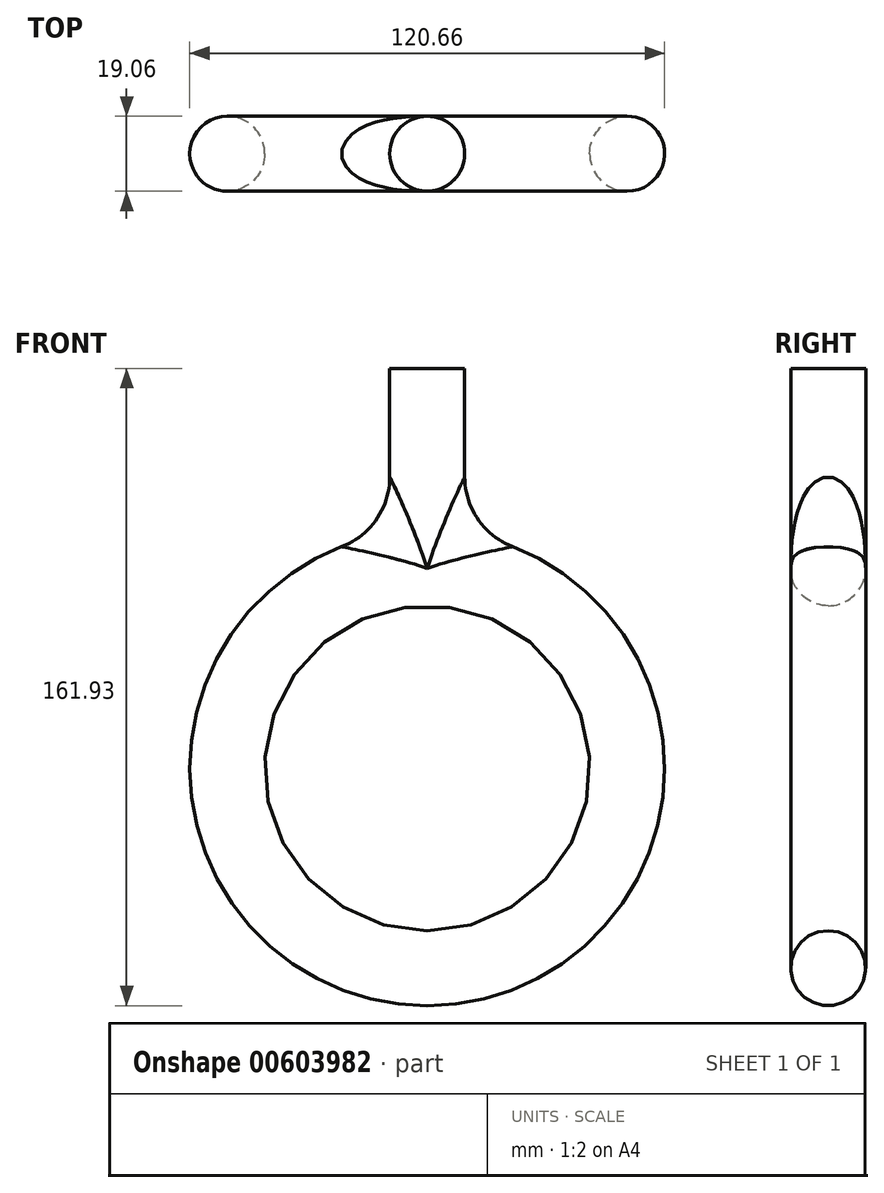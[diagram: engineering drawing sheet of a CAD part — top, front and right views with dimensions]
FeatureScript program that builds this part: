
annotation { "Feature Type Name" : "Feature", "Feature Type Description" : "" }
export const myFeature = defineFeature(function(context is Context, id is Id, definition is map)
    precondition{}
    {
        {
            var Q0;
            Q0=qCreatedBy(makeId("Top.planeOp"),FACE);
            var sketch = newSketch(context, id + "F0", { "sketchPlane" : qUnion([Q0])});
            skCircle(sketch, "E0", {"center": v(0, 0) * mm, "radius": 9.52 * mm});
            skSolve(sketch);
        }
        {
            var Q0;
            Q0 = qSketchRegion(id + "F0", true);
            extrude(context, id + "F1", {"entities" : qUnion([Q0]), "depth" : 50.8 * mm, "offsetDistance" : 25.4 * mm});
        }
        {
            var Q0;
            Q0=qCreatedBy(makeId("Right.planeOp"),FACE);
            var sketch = newSketch(context, id + "F2", { "sketchPlane" : qUnion([Q0])});
            skCircle(sketch, "E1", {"center": v(0, 0) * mm, "radius": 9.53 * mm});
            skSolve(sketch);
        }
        {
            var Q0;
            Q0=qCreatedBy(makeId("Front.planeOp"),FACE);
            var sketch = newSketch(context, id + "F3", { "sketchPlane" : qUnion([Q0])});
            skCircle(sketch, "E2", {"center": v(0, -50.8) * mm, "radius": 50.8 * mm});
            skSolve(sketch);
        }
        {
            var Q0;
            Q0=makeQuery(id+"F2.imprint","IMPRINT",FACE,{"disambiguationData":[TD([[makeQuery(id+"F2.imprint","IMPRINT",EDGE,{"derivedFrom":sQuery(id+"F2.wireOp",EDGE,"E1")}),1.0]])]});
            var Q1;
            Q1=sQuery(id+"F3.wireOp",EDGE,"E2");
            revolve(context, id + "F4", {"operationType" : NewBodyOperationType.ADD, "entities" : qUnion([Q0]), "axis" : qUnion([Q1]), "revolveType" : RevolveType.FULL});
        }
        {
            var Q0;
            Q0=makeQuery(id+"F4.boolean.opBoolean","INTERSECT",EDGE,{"disambiguationData":[OD(0.0)],"derivedFrom":[makeQuery(id+"F1.opExtrude","SWEPT_FACE",FACE,{"disambiguationData":[OSD([sQuery(id+"F0.wireOp",EDGE,"E0")])]}),makeQuery(id+"F4.opRevolve","SWEPT_FACE",FACE,{"disambiguationData":[OSD([sQuery(id+"F2.wireOp",EDGE,"E1")])]})]});
            var Q1;
            Q1=makeQuery(id+"F4.boolean.opBoolean","INTERSECT",EDGE,{"disambiguationData":[OD(1.0)],"derivedFrom":[makeQuery(id+"F1.opExtrude","SWEPT_FACE",FACE,{"disambiguationData":[OSD([sQuery(id+"F0.wireOp",EDGE,"E0")])]}),makeQuery(id+"F4.opRevolve","SWEPT_FACE",FACE,{"disambiguationData":[OSD([sQuery(id+"F2.wireOp",EDGE,"E1")])]})]});
            fillet(context, id + "F5", {"entities" : qUnion([Q0, Q1]), "radius" : 19.05 * mm, "tangentPropagation" : true, "allowEdgeOverflow" : false});
        }
    });
